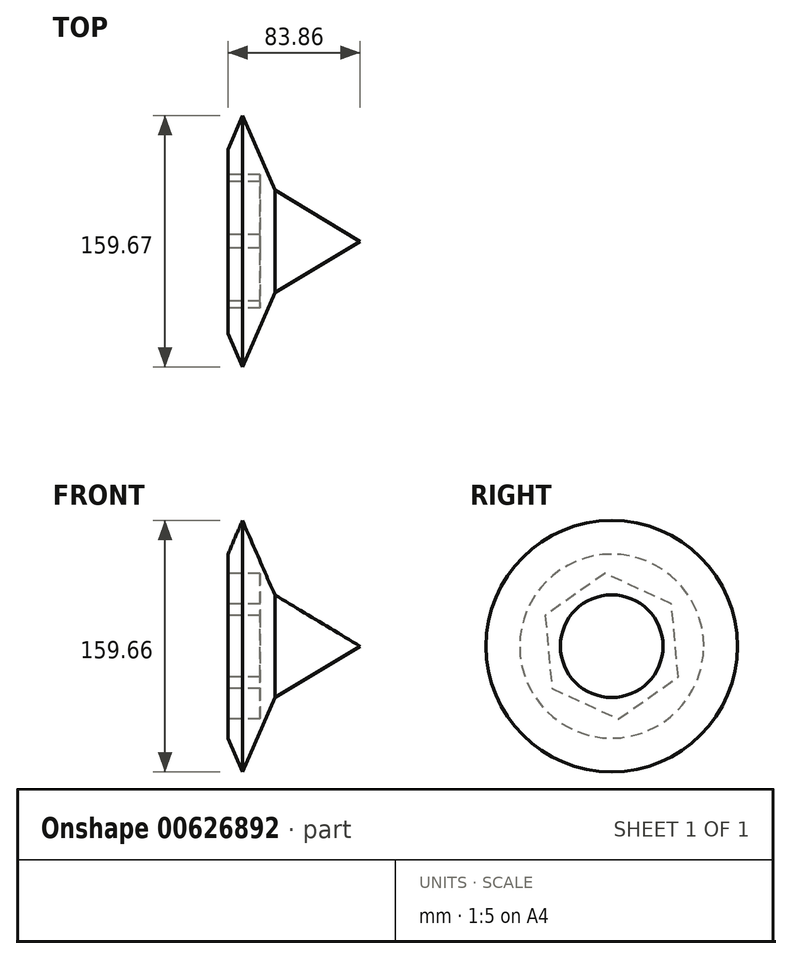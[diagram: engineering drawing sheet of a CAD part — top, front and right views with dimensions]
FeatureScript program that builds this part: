
annotation { "Feature Type Name" : "Feature", "Feature Type Description" : "" }
export const myFeature = defineFeature(function(context is Context, id is Id, definition is map)
    precondition{}
    {
        {
            var Q0;
            Q0=qCreatedBy(makeId("Top.planeOp"),FACE);
            var sketch = newSketch(context, id + "F0", { "sketchPlane" : qUnion([Q0])});
            skLineSegment(sketch, "E0", {"start": v(-113.92, 13.06) * mm, "end": v(-113.92, -45.37) * mm});
            skLineSegment(sketch, "E1", {"start": v(-113.92, -45.37) * mm, "end": v(-30.06, -45.37) * mm});
            skLineSegment(sketch, "E2", {"start": v(-30.06, -45.37) * mm, "end": v(-84.22, -12.79) * mm});
            skLineSegment(sketch, "E3", {"start": v(-84.22, -12.79) * mm, "end": v(-104.78, 34.47) * mm});
            skLineSegment(sketch, "E4", {"start": v(-104.78, 34.47) * mm, "end": v(-113.92, 13.06) * mm});
            skSolve(sketch);
        }
        {
            var Q0;
            Q0=makeQuery(id+"F0.imprint","IMPRINT",FACE,{"disambiguationData":[TD([[makeQuery(id+"F0.imprint","IMPRINT",EDGE,{"derivedFrom":sQuery(id+"F0.wireOp",EDGE,"E0")}),1.0]])]});
            var Q1;
            Q1=sQuery(id+"F0.wireOp",EDGE,"E1");
            revolve(context, id + "F1", {"entities" : qUnion([Q0]), "axis" : qUnion([Q1]), "revolveType" : RevolveType.FULL});
        }
        {
            var Q0;
            Q0=makeQuery(id+"F1.opRevolve","SWEPT_FACE",FACE,{"disambiguationData":[OSD([sQuery(id+"F0.wireOp",EDGE,"E0")])]});
            var sketch = newSketch(context, id + "F2", { "sketchPlane" : qUnion([Q0])});
            skCircle(sketch, "E5.cCircle", {"center": v(45.37, 0) * mm, "radius": 40.29 * mm, "construction": true});
            skLineSegment(sketch, "E5.0", {"start": v(87.63, 19.44) * mm, "end": v(83.33, -26.88) * mm});
            skLineSegment(sketch, "E5.1", {"start": v(83.33, -26.88) * mm, "end": v(41.07, -46.32) * mm});
            skLineSegment(sketch, "E5.2", {"start": v(41.07, -46.32) * mm, "end": v(3.1, -19.44) * mm});
            skLineSegment(sketch, "E5.3", {"start": v(3.1, -19.44) * mm, "end": v(7.4, 26.88) * mm});
            skLineSegment(sketch, "E5.4", {"start": v(7.4, 26.88) * mm, "end": v(49.66, 46.32) * mm});
            skLineSegment(sketch, "E5.5", {"start": v(49.66, 46.32) * mm, "end": v(87.63, 19.44) * mm});
            skPoint(sketch, "E5.0.midPoint", {"position": v(85.48, -3.72) * mm});
            skSolve(sketch);
        }
        {
            var Q0;
            Q0=makeQuery(id+"F2.imprint","IMPRINT",FACE,{"disambiguationData":[TD([[makeQuery(id+"F2.imprint","IMPRINT",EDGE,{"derivedFrom":sQuery(id+"F2.wireOp",EDGE,"E5.0")}),-1.0]])]});
            extrude(context, id + "F3", {"entities" : qUnion([Q0]), "operationType" : NewBodyOperationType.REMOVE, "oppositeDirection" : true, "depth" : 20.32 * mm, "offsetDistance" : 25.4 * mm});
        }
    });
